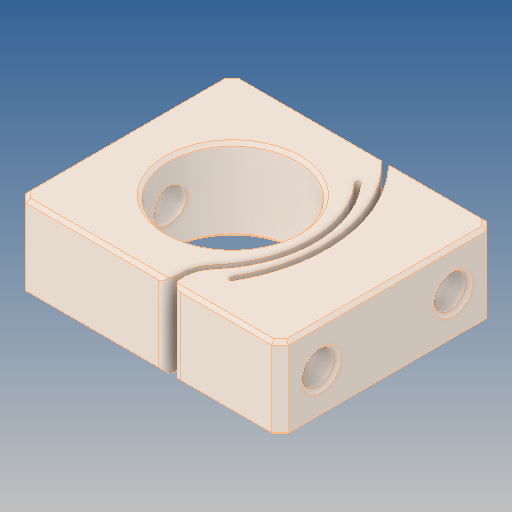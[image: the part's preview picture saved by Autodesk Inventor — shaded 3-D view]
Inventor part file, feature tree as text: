
AUTODESK INVENTOR PART (.ipt)
format: ipt  version: 2019 (Build 230136000, 136)  size: 180,224 bytes
history: native  units: mm
features: chamfer x1
ambient origin geometry x8: Origin, YZ Plane, XZ Plane, XY Plane, X Axis, Y Axis, Z Axis, Center Point
bodies: Solid1 (feature_tree)
feature tree (1):
  chamfer  "Chamfer2 - .01x45deg"  [1 undecoded]
note: 1 required parameter value undecoded (feature->parameter linkage not recoverable at this tier; creation-order binding heuristic only, values carry confidence <= 0.55)
